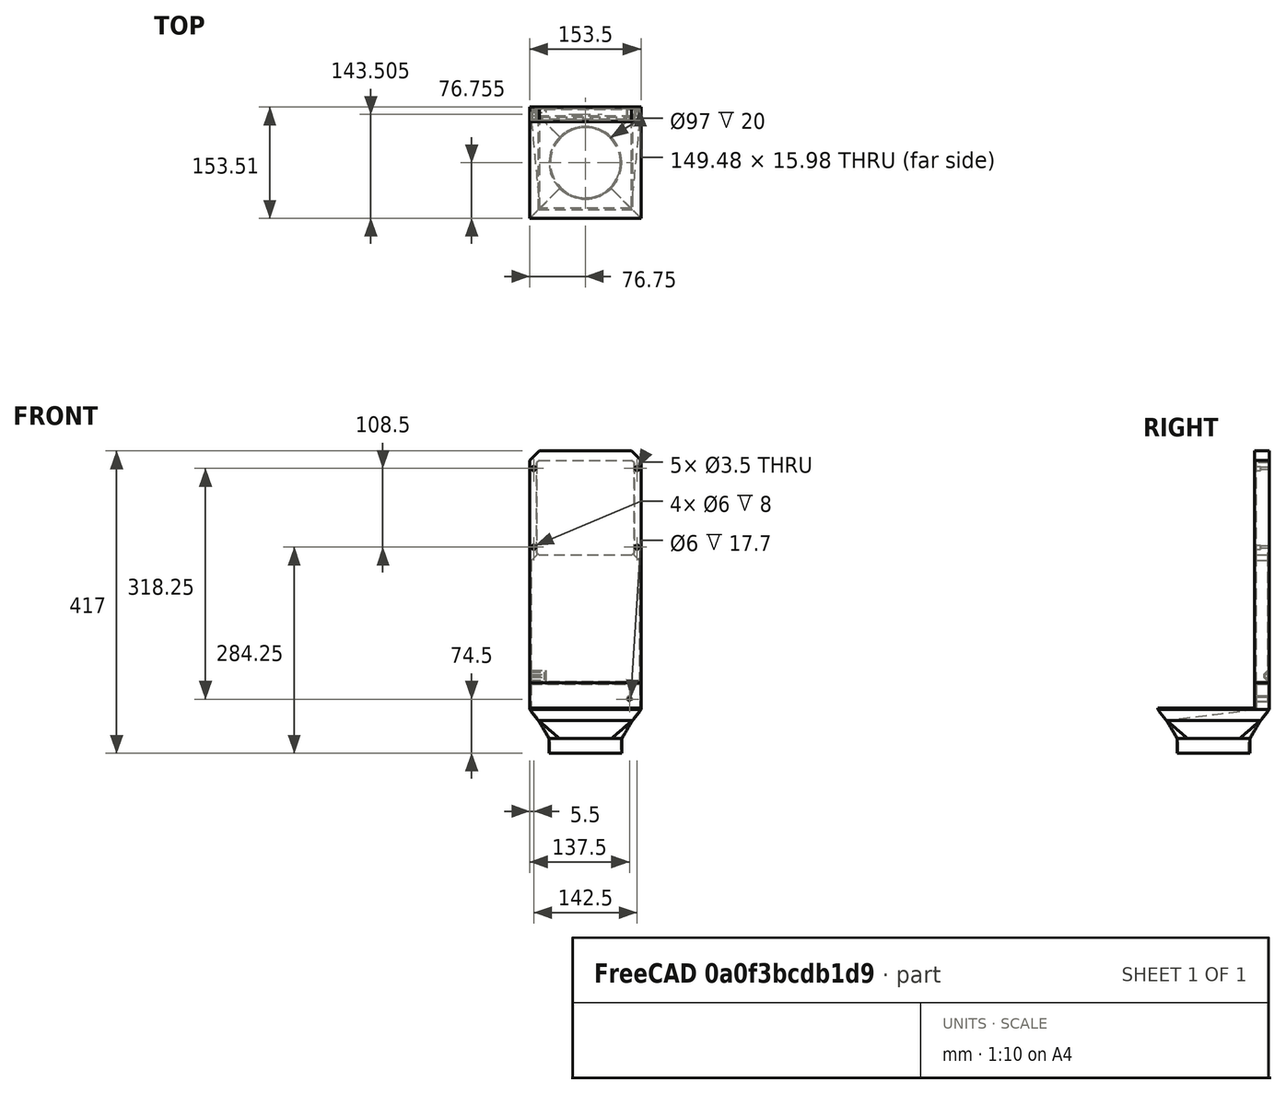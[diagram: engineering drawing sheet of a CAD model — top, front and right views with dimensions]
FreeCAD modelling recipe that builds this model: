
FCSTD DOCUMENT  (FreeCAD 1.1R20260108 (Git shallow))
Label: H2C Vertical Exhaust
License: Creative Commons Attribution 4.0
LicenseURL: https://creativecommons.org/licenses/by/4.0/
objects: Sketcher::SketchObject×14, PartDesign::Pad×9, PartDesign::Pocket×5, App::Point×3, PartDesign::Body×2, PartDesign::Chamfer×2, PartDesign::AdditiveLoft×2, App::Link×2, App::FeaturePython×2, Part::FeaturePython×2, PartDesign::SubShapeBinder×1, PartDesign::Plane×1, Assembly::JointGroup×1, Assembly::AssemblyObject×1, App::VarSet×1
note: 88 computed .brp shape members not serialized (recipe doc carries the construction recipe); baked Part::Feature solids carry a one-line shape summary decoded from their .brp

FEATURE [Sketcher::SketchObject] Sketch
  ArcFitTolerance = 1e-06
  AttachmentSupport = -> [XZ_Plane]
  ExternalTypes = [0]
  FullyConstrained = true
  MakeInternals = false
  MapMode = 5
  Placement = pos=(0,0,0) rot=(1,0,0;1.5708rad)
  sketch-geometry (25):
    g0: LineSegment StartX=-76.75 StartY=-241.5 StartZ=0 EndX=76.75 EndY=-241.5 EndZ=0
    g1: LineSegment StartX=76.75 StartY=-241.5 StartZ=0 EndX=76.75 EndY=65.5 EndZ=0
    g2: LineSegment StartX=63.75 StartY=78.5 StartZ=0 EndX=-63.75 EndY=78.5 EndZ=0
    g3: LineSegment StartX=-76.75 StartY=65.5 StartZ=0 EndX=-76.75 EndY=-241.5 EndZ=0
    g4: GeomPoint X=0 Y=0 Z=0
    g5: GeomPoint X=-76.75 Y=78.5 Z=0
    g6: GeomPoint X=76.75 Y=78.5 Z=0
    g7: LineSegment StartX=-63.75 StartY=-65.5 StartZ=0 EndX=63.75 EndY=-65.5 EndZ=0
    g8: LineSegment StartX=67.25 StartY=-62 StartZ=0 EndX=67.25 EndY=62 EndZ=0
    g9: LineSegment StartX=63.75 StartY=65.5 StartZ=0 EndX=-63.75 EndY=65.5 EndZ=0
    g10: LineSegment StartX=-67.25 StartY=62 StartZ=0 EndX=-67.25 EndY=-62 EndZ=0
    g11: GeomPoint X=0 Y=0 Z=0
    g12: GeomPoint X=-67.25 Y=65.5 Z=0
    g13: GeomPoint X=67.25 Y=65.5 Z=0
    g14: GeomPoint X=67.25 Y=-62 Z=0
    g15: Circle CenterX=-71.25 CenterY=54.25 CenterZ=0 NormalX=0 NormalY=0 NormalZ=1 AngleXU=0 Radius=1.75
    g16: Circle CenterX=71.25 CenterY=54.25 CenterZ=0 NormalX=0 NormalY=0 NormalZ=1 AngleXU=0 Radius=1.75
    g17: Circle CenterX=71.25 CenterY=-54.25 CenterZ=0 NormalX=0 NormalY=0 NormalZ=1 AngleXU=0 Radius=1.75
    g18: Circle CenterX=-71.25 CenterY=-54.25 CenterZ=0 NormalX=0 NormalY=0 NormalZ=1 AngleXU=0 Radius=1.75
    g19: LineSegment StartX=-76.75 StartY=65.5 StartZ=0 EndX=-63.75 EndY=78.5 EndZ=0
    g20: LineSegment StartX=63.75 StartY=78.5 StartZ=0 EndX=76.75 EndY=65.5 EndZ=0
    g21: LineSegment StartX=-67.25 StartY=62 StartZ=0 EndX=-63.75 EndY=65.5 EndZ=0
    g22: LineSegment StartX=63.75 StartY=65.5 StartZ=0 EndX=67.25 EndY=62 EndZ=0
    g23: LineSegment StartX=-67.25 StartY=-62 StartZ=0 EndX=-63.75 EndY=-65.5 EndZ=0
    g24: LineSegment StartX=63.75 StartY=-65.5 StartZ=0 EndX=67.25 EndY=-62 EndZ=0
  constraints (59):
    c: Horizontal(g0)
    c: Vertical(g3)
    c: Coincident(g4,g-1)
    c: DistanceX(g5,g6) = 153.5
    c: PointOnObject(g5,g3)
    c: PointOnObject(g5,g2)
    c: PointOnObject(g6,g2)
    c: PointOnObject(g6,g1)
    c: Horizontal(g7)
    c: Coincident(g11,g4)
    c: DistanceX(g12,g13) = 134.5
    c: DistanceY(g14,g13) = 127.5
    c: PointOnObject(g12,g10)
    c: PointOnObject(g12,g9)
    c: PointOnObject(g13,g9)
    c: PointOnObject(g13,g8)
    c: Horizontal(g15,g16)
    c: Horizontal(g18,g17)
    c: Vertical(g16,g17)
    c: Vertical(g15,g18)
    c: DistanceX(g15,g16) = 142.5
    c: DistanceY(g17,g16) = 108.5
    c: Symmetric(g18,g16,g4)
    c: Equal(g15,g16)
    c: Equal(g15,g18)
    c: Equal(g15,g17)
    c: Diameter(g15) = 3.5
    c: Vertical(g10)
    c: Coincident(g14,g8)
    c: Coincident(g1,g0)
    c: Coincident(g0,g3)
    c: DistanceY(g0,g2) = 320
    c: Coincident(g19,g3)
    c: Coincident(g19,g2)
    c: Coincident(g20,g2)
    c: Coincident(g20,g1)
    c: Symmetric(g2,g2,g-2)
    c: Symmetric(g3,g1,g-2)
    c: DistanceX(g3,g9) = 13
    c: Horizontal(g3,g9)
    c: Vertical(g2,g9)
    c: Coincident(g21,g10)
    c: Coincident(g21,g9)
    c: Coincident(g22,g9)
    c: Coincident(g22,g8)
    c: Angle(g19,g3) = 0.785398
    c: Angle(g21,g10) = 0.785398
    c: Symmetric(g9,g9,g-2)
    c: Symmetric(g8,g10,g-2)
    c: Vertical(g7,g9)
    c: Coincident(g23,g10)
    c: Coincident(g23,g7)
    c: Coincident(g24,g7)
    c: Coincident(g24,g8)
    c: Vertical(g7,g9)
    c: Horizontal(g10,g8)
    c: Angle(g10,g23) = 0.785398
    c: Symmetric(g8,g10,g4)
    c: Vertical(g1)
FEATURE [PartDesign::Pad] Pad  label="Surface against printer"
  Direction = (0,-1,2e-16)
  Length = 2
  Length2 = 10
  Placement = pos=(0,0,0) rot=(1,0,0;1.5708rad)
  Profile = -> Sketch
  ReferenceAxis = -> Sketch [N_Axis]
  SideType = 0
  Suppressed = false
  Type = 0
  Type2 = 0
FEATURE [Sketcher::SketchObject] Sketch011
  ArcFitTolerance = 1e-06
  AttachmentSupport = -> [Pad]
  ExternalGeometry = -> [Pad]
  ExternalTypes = [0]
  FullyConstrained = true
  MakeInternals = false
  MapMode = 5
  Placement = pos=(0,-1.17e-14,0) rot=(-1,0,0;1.5708rad)
  sketch-geometry (16):
    g0: LineSegment StartX=-76.75 StartY=-65.5 StartZ=0 EndX=-76.75 EndY=241.5 EndZ=0
    g1: LineSegment StartX=-76.75 StartY=241.5 StartZ=0 EndX=-74.75 EndY=241.5 EndZ=0
    g2: LineSegment StartX=-74.75 StartY=241.5 StartZ=0 EndX=-74.75 EndY=73 EndZ=0
    g3: LineSegment StartX=-74.75 StartY=73 StartZ=0 EndX=-67.25 EndY=65.5 EndZ=0
    g4: LineSegment StartX=-67.25 StartY=65.5 StartZ=0 EndX=-67.25 EndY=-62 EndZ=0
    g5: LineSegment StartX=-67.25 StartY=-62 StartZ=0 EndX=-63.75 EndY=-65.5 EndZ=0
    g6: LineSegment StartX=-63.75 StartY=-65.5 StartZ=0 EndX=63.75 EndY=-65.5 EndZ=0
    g7: LineSegment StartX=63.75 StartY=-65.5 StartZ=0 EndX=67.25 EndY=-62 EndZ=0
    g8: LineSegment StartX=67.25 StartY=-62 StartZ=0 EndX=67.25 EndY=65.5 EndZ=0
    g9: LineSegment StartX=67.25 StartY=65.5 StartZ=0 EndX=74.75 EndY=73 EndZ=0
    g10: LineSegment StartX=74.75 StartY=73 StartZ=0 EndX=74.75 EndY=241.5 EndZ=0
    g11: LineSegment StartX=74.75 StartY=241.5 StartZ=0 EndX=76.75 EndY=241.5 EndZ=0
    g12: LineSegment StartX=76.75 StartY=241.5 StartZ=0 EndX=76.75 EndY=-65.5 EndZ=0
    g13: LineSegment StartX=76.75 StartY=-65.5 StartZ=0 EndX=63.75 EndY=-78.5 EndZ=0
    g14: LineSegment StartX=63.75 StartY=-78.5 StartZ=0 EndX=-63.75 EndY=-78.5 EndZ=0
    g15: LineSegment StartX=-63.75 StartY=-78.5 StartZ=0 EndX=-76.75 EndY=-65.5 EndZ=0
  constraints (38):
    c: Coincident(g-6,g0)
    c: Coincident(g0,g-7)
    c: Coincident(g0,g1)
    c: PointOnObject(g1,g-7)
    c: Coincident(g1,g2)
    c: Vertical(g2)
    c: Coincident(g2,g3)
    c: Coincident(g3,g4)
    c: Coincident(g4,g-3)
    c: PointOnObject(g-3,g4)
    c: DistanceX(g1,g1) = 2
    c: Angle(g2,g3) = 0.785398
    c: PointOnObject(g3,g-8)
    c: Coincident(g4,g5)
    c: Coincident(g5,g-9)
    c: Coincident(g5,g6)
    c: Coincident(g6,g-9)
    c: Coincident(g6,g7)
    c: Coincident(g7,g-4)
    c: Coincident(g7,g8)
    c: Vertical(g8)
    c: Coincident(g8,g9)
    c: Coincident(g9,g10)
    c: PointOnObject(g10,g-7)
    c: Vertical(g10)
    c: Coincident(g10,g11)
    c: Coincident(g11,g-7)
    c: Coincident(g11,g12)
    c: Coincident(g12,g-5)
    c: Coincident(g12,g13)
    c: Coincident(g13,g-5)
    c: Coincident(g13,g14)
    c: Coincident(g14,g-6)
    c: Coincident(g14,g15)
    c: Coincident(g15,g0)
    c: Angle(g9,g10) = 0.785398
    c: PointOnObject(g8,g-8)
    c: Equal(g11,g1)
FEATURE [PartDesign::Pad] Pad006  label="Duct walls"
  BaseFeature = -> Pad
  Direction = (0,1,2e-16)
  Length = 16
  Length2 = 10
  Placement = pos=(0,0,0) rot=(1,0,0;1.5708rad)
  Profile = -> Sketch011
  ReferenceAxis = -> Sketch011 [N_Axis]
  Refine = true
  SideType = 0
  Suppressed = false
  Type = 0
  Type2 = 0
FEATURE [Sketcher::SketchObject] Sketch012
  ArcFitTolerance = 1e-06
  AttachmentSupport = -> [Pad006]
  ExternalGeometry = -> [Pad006]
  ExternalTypes = [0]
  FullyConstrained = true
  MakeInternals = false
  MapMode = 5
  Placement = pos=(0,16,0) rot=(-1,0,0;1.5708rad)
  sketch-geometry (6):
    g0: LineSegment StartX=-76.75 StartY=241.5 StartZ=0 EndX=-76.75 EndY=-65.5 EndZ=0
    g1: LineSegment StartX=-76.75 StartY=-65.5 StartZ=0 EndX=-63.75 EndY=-78.5 EndZ=0
    g2: LineSegment StartX=-63.75 StartY=-78.5 StartZ=0 EndX=63.75 EndY=-78.5 EndZ=0
    g3: LineSegment StartX=63.75 StartY=-78.5 StartZ=0 EndX=76.75 EndY=-65.5 EndZ=0
    g4: LineSegment StartX=76.75 StartY=-65.5 StartZ=0 EndX=76.75 EndY=241.5 EndZ=0
    g5: LineSegment StartX=76.75 StartY=241.5 StartZ=0 EndX=-76.75 EndY=241.5 EndZ=0
  constraints (12):
    c: Coincident(g-3,g0)
    c: Coincident(g0,g-3)
    c: Coincident(g0,g1)
    c: Coincident(g1,g-5)
    c: Coincident(g1,g2)
    c: Coincident(g2,g-5)
    c: Coincident(g2,g3)
    c: Coincident(g3,g-4)
    c: Coincident(g3,g4)
    c: Coincident(g4,g-4)
    c: Coincident(g4,g5)
    c: Coincident(g5,g0)
FEATURE [PartDesign::Pad] Pad007  label="Surface away from printer"
  BaseFeature = -> Pad006
  Direction = (0,1,2e-16)
  Length = 2
  Length2 = 10
  Placement = pos=(0,0,0) rot=(1,0,0;1.5708rad)
  Profile = -> Sketch012
  ReferenceAxis = -> Sketch012 [N_Axis]
  Refine = true
  SideType = 0
  Suppressed = false
  Type = 0
  Type2 = 0
FEATURE [Sketcher::SketchObject] Sketch003
  ArcFitTolerance = 1e-06
  AttachmentOffset = pos=(0,0,6) rot=(0,0,1;0rad)
  AttachmentSupport = -> [Pad007]
  ExternalTypes = [0]
  FullyConstrained = true
  MakeInternals = false
  MapMode = 5
  Placement = pos=(0,10,1.3e-15) rot=(1,0,0;1.5708rad)
  sketch-geometry (4):
    g0: Circle CenterX=71.25 CenterY=54.25 CenterZ=0 NormalX=0 NormalY=0 NormalZ=1 AngleXU=0 Radius=3
    g1: Circle CenterX=-71.25 CenterY=54.25 CenterZ=0 NormalX=0 NormalY=0 NormalZ=1 AngleXU=0 Radius=3
    g2: Circle CenterX=-71.25 CenterY=-54.25 CenterZ=0 NormalX=0 NormalY=0 NormalZ=1 AngleXU=0 Radius=3
    g3: Circle CenterX=71.25 CenterY=-54.25 CenterZ=0 NormalX=0 NormalY=0 NormalZ=1 AngleXU=0 Radius=3
  constraints (8):
    c: Coincident(g0,g-4)
    c: Coincident(g1,g-3)
    c: Coincident(g2,g-6)
    c: Coincident(g3,g-5)
    c: Equal(g3,g2)
    c: Equal(g0,g1)
    c: Equal(g1,g2)
    c: Diameter(g3) = 6
FEATURE [PartDesign::Pocket] Pocket  label="Screw head pockets"
  BaseFeature = -> Pad007
  Direction = (0,1,-2e-16)
  Length = 5
  Length2 = 5
  Placement = pos=(0,0,0) rot=(1,0,0;1.5708rad)
  Profile = -> Sketch003
  ReferenceAxis = -> Sketch003 [N_Axis]
  SideType = 0
  Suppressed = false
  Type = 1
  Type2 = 0
FEATURE [PartDesign::Pocket] Pocket001  label="Screw pockets"
  BaseFeature = -> Pocket
  Direction = (0,-1,0)
  Length = 5
  Length2 = 5
  Placement = pos=(0,0,0) rot=(1,0,0;1.5708rad)
  Profile = -> Pocket [Edge44,Edge45,Edge46,Edge43]
  Reversed = true
  SideType = 0
  Suppressed = false
  Type = 1
  Type2 = 0
FEATURE [Sketcher::SketchObject] Sketch013
  ArcFitTolerance = 1e-06
  AttachmentSupport = -> [Pocket001]
  ExternalGeometry = -> [Pocket001]
  ExternalTypes = [0]
  FullyConstrained = true
  MakeInternals = false
  MapMode = 5
  Placement = pos=(76.75,0,0) rot=(0.707107,0,0.707107;3.14159rad)
  sketch-geometry (7):
    g0: LineSegment StartX=-239.5 StartY=2 StartZ=0 EndX=-239.5 EndY=1.572e-13 EndZ=0
    g1: LineSegment StartX=-239.5 StartY=1.572e-13 StartZ=0 EndX=-234 EndY=-5.5 EndZ=0
    g2: LineSegment StartX=-234 StartY=-5.5 StartZ=0 EndX=-230 EndY=-5.5 EndZ=0
    g3: LineSegment StartX=-230 StartY=-5.5 StartZ=0 EndX=-224.5 EndY=1.572e-13 EndZ=0
    g4: LineSegment StartX=-224.5 StartY=1.572e-13 StartZ=0 EndX=-224.5 EndY=2 EndZ=0
    g5: LineSegment StartX=-224.5 StartY=2 StartZ=0 EndX=-239.5 EndY=2 EndZ=0
    g6: GeomPoint X=-54.25 Y=2 Z=0
  constraints (19):
    c: PointOnObject(g0,g-4)
    c: Vertical(g0)
    c: Coincident(g0,g1)
    c: Coincident(g1,g2)
    c: Horizontal(g2)
    c: Coincident(g2,g3)
    c: Coincident(g3,g4)
    c: PointOnObject(g4,g-4)
    c: Vertical(g4)
    c: Coincident(g4,g5)
    c: Coincident(g5,g0)
    c: Angle(g0,g1) = 0.785398
    c: Angle(g3,g4) = 0.785398
    c: DistanceX(g5,g5) = 15
    c: DistanceY(g2,g4) = 7.5
    c: DistanceY(g4,g4) = 2
    c: Symmetric(g-3,g-3,g6)
    c: Horizontal(g0,g3)
    c: DistanceX(g4,g6) = 170.25
FEATURE [PartDesign::Pad] Pad008  label="Filament tube walls"
  BaseFeature = -> Pocket001
  Direction = (1,0,-2e-16)
  Length = 22
  Length2 = 10
  Placement = pos=(0,0,0) rot=(1,0,0;1.5708rad)
  Profile = -> Sketch013
  ReferenceAxis = -> Sketch013 [N_Axis]
  Refine = true
  Reversed = true
  SideType = 0
  Suppressed = false
  Type = 0
  Type2 = 0
FEATURE [Sketcher::SketchObject] Sketch014
  ArcFitTolerance = 1e-06
  AttachmentSupport = -> [Pad008]
  ExternalGeometry = -> [Sketch013]
  ExternalTypes = [0]
  FullyConstrained = true
  MakeInternals = false
  MapMode = 5
  Placement = pos=(76.75,0,0) rot=(0.707107,0,0.707107;3.14159rad)
  sketch-geometry (7):
    g0: LineSegment StartX=-237.5 StartY=2 StartZ=0 EndX=-237.5 EndY=0.828427 EndZ=0
    g1: LineSegment StartX=-237.5 StartY=0.828427 StartZ=0 EndX=-233.172 EndY=-3.5 EndZ=0
    g2: LineSegment StartX=-233.172 StartY=-3.5 StartZ=0 EndX=-230.828 EndY=-3.5 EndZ=0
    g3: LineSegment StartX=-230.828 StartY=-3.5 StartZ=0 EndX=-226.5 EndY=0.828427 EndZ=0
    g4: LineSegment StartX=-226.5 StartY=0.828427 StartZ=0 EndX=-226.5 EndY=2 EndZ=0
    g5: LineSegment StartX=-226.5 StartY=2 StartZ=0 EndX=-237.5 EndY=2 EndZ=0
    g6: LineSegment StartX=-230 StartY=-5.5 StartZ=0 EndX=-230.828 EndY=-3.5 EndZ=0
  constraints (20):
    c: PointOnObject(g0,g-3)
    c: Vertical(g0)
    c: Coincident(g0,g1)
    c: Coincident(g1,g2)
    c: Horizontal(g2)
    c: Coincident(g2,g3)
    c: Coincident(g3,g4)
    c: PointOnObject(g4,g-3)
    c: Vertical(g4)
    c: Coincident(g4,g5)
    c: Coincident(g5,g0)
    c: Angle(g0,g1) = 0.785398
    c: Angle(g3,g4) = 0.785398
    c: DistanceX(g-3,g0) = 2
    c: DistanceX(g4,g-3) = 2
    c: DistanceY(g-4,g2) = 2
    c: Horizontal(g0,g3)
    c: Coincident(g6,g-4)
    c: Coincident(g6,g2)
    c: Angle(g6,g-4) = 1.1781
FEATURE [PartDesign::Pocket] Pocket002  label="Filament tube opening"
  BaseFeature = -> Pad008
  Direction = (-1,0,2e-16)
  Length = 20
  Length2 = 5
  Placement = pos=(0,0,0) rot=(1,0,0;1.5708rad)
  Profile = -> Sketch014 [Edge3,Edge2,Edge1,Edge7,Edge6,Edge5]
  ReferenceAxis = -> Sketch014 [N_Axis]
  SideType = 0
  Suppressed = false
  Type = 0
  Type2 = 0
FEATURE [PartDesign::Body] Body  label="Back of printer"
  AllowCompound = false
  Group = -> [Sketch,Pad,Pad006,Pad007,Pocket,Pocket001,Sketch003,Sketch011,Sketch012,Sketch013,Pad008,Sketch014,Pocket002]
  Origin = -> Origin
  Placement = pos=(2e-15,15.975,0) rot=(0,0,1;3.14159rad)
  Tip = -> Pocket002
FEATURE [PartDesign::SubShapeBinder] Binder  label="Duct opening binder"
  BindCopyOnChange = 0
  BindMode = 0
  ClaimChildren = false
  Context = -> Body001 [Binder.]
  Fuse = false
  MakeFace = true
  OffsetFill = false
  OffsetIntersection = false
  OffsetJoinType = 0
  OffsetOpenResult = false
  PartialLoad = false
  Relative = true
  Support = -> [Body[Pocket002.Face3]]
  _Version = 2
FEATURE [PartDesign::Plane] DatumPlane  label="Duct opening plane"
  AttachmentSupport = -> [Binder]
  Length = 184.895
  MapMode = 13
  Placement = pos=(25.5833,4.64167,-241.5) rot=(0,0,1;0rad)
  ResizeMode = 0
  Width = 191.92
FEATURE [Sketcher::SketchObject] Sketch015
  ArcFitTolerance = 1e-06
  AttachmentSupport = -> [DatumPlane]
  ExternalGeometry = -> [Binder]
  ExternalTypes = [0]
  FullyConstrained = true
  MakeInternals = false
  MapMode = 5
  Placement = pos=(25.5833,4.64167,-241.5) rot=(0,0,1;0rad)
  sketch-geometry (8):
    g0: LineSegment StartX=49.1667 StartY=-4.66667 StartZ=0 EndX=49.1667 EndY=11.3333 EndZ=0
    g1: LineSegment StartX=49.1667 StartY=11.3333 StartZ=0 EndX=-100.333 EndY=11.3333 EndZ=0
    g2: LineSegment StartX=-100.333 StartY=11.3333 StartZ=0 EndX=-100.333 EndY=-4.66667 EndZ=0
    g3: LineSegment StartX=-100.333 StartY=-4.66667 StartZ=0 EndX=49.1667 EndY=-4.66667 EndZ=0
    g4: LineSegment StartX=51.1667 StartY=-6.66667 StartZ=0 EndX=51.1667 EndY=13.3333 EndZ=0
    g5: LineSegment StartX=51.1667 StartY=13.3333 StartZ=0 EndX=-102.333 EndY=13.3333 EndZ=0
    g6: LineSegment StartX=-102.333 StartY=13.3333 StartZ=0 EndX=-102.333 EndY=-6.66667 EndZ=0
    g7: LineSegment StartX=-102.333 StartY=-6.66667 StartZ=0 EndX=51.1667 EndY=-6.66667 EndZ=0
  constraints (20):
    c: Coincident(g0,g1)
    c: Coincident(g1,g2)
    c: Coincident(g2,g3)
    c: Coincident(g3,g0)
    c: Vertical(g0)
    c: Vertical(g2)
    c: Horizontal(g1)
    c: Horizontal(g3)
    c: Coincident(g0,g-4)
    c: Coincident(g1,g-5)
    c: Coincident(g4,g5)
    c: Coincident(g5,g6)
    c: Coincident(g6,g7)
    c: Coincident(g7,g4)
    c: Vertical(g4)
    c: Vertical(g6)
    c: Horizontal(g5)
    c: Horizontal(g7)
    c: Coincident(g4,g-3)
    c: Coincident(g5,g-6)
FEATURE [PartDesign::Pad] Pad009  label="Tube extension to top of printer"
  Direction = (0,-4.3e-15,1)
  Length = 35
  Length2 = 10
  Placement = pos=(25.5833,4.64167,-241.5) rot=(0,0,1;0rad)
  Profile = -> Sketch015
  ReferenceAxis = -> Sketch015 [N_Axis]
  Reversed = true
  SideType = 0
  Suppressed = false
  Type = 0
  Type2 = 0
FEATURE [Sketcher::SketchObject] Sketch016
  ArcFitTolerance = 1e-06
  AttachmentSupport = -> [Pad009]
  ExternalGeometry = -> [Pad009]
  ExternalTypes = [0]
  FullyConstrained = true
  MakeInternals = false
  MapMode = 5
  Placement = pos=(25.5833,4.64167,-241.5) rot=(0,0,1;0rad)
  sketch-geometry (9):
    g0: LineSegment StartX=49.1667 StartY=-4.66667 StartZ=0 EndX=49.1667 EndY=11.3333 EndZ=0
    g1: LineSegment StartX=49.1667 StartY=11.3333 StartZ=0 EndX=-100.333 EndY=11.3333 EndZ=0
    g2: LineSegment StartX=-100.333 StartY=11.3333 StartZ=0 EndX=-100.333 EndY=-4.66667 EndZ=0
    g3: LineSegment StartX=-100.333 StartY=-4.66667 StartZ=0 EndX=49.1667 EndY=-4.66667 EndZ=0
    g4: LineSegment StartX=47.6667 StartY=-3.16667 StartZ=0 EndX=47.6667 EndY=9.83333 EndZ=0
    g5: LineSegment StartX=47.6667 StartY=9.83333 StartZ=0 EndX=-98.8333 EndY=9.83333 EndZ=0
    g6: LineSegment StartX=-98.8333 StartY=9.83333 StartZ=0 EndX=-98.8333 EndY=-3.16667 EndZ=0
    g7: LineSegment StartX=-98.8333 StartY=-3.16667 StartZ=0 EndX=47.6667 EndY=-3.16667 EndZ=0
    g8: GeomPoint X=-25.5833 Y=3.33333 Z=0
  constraints (22):
    c: Coincident(g0,g1)
    c: Coincident(g1,g2)
    c: Coincident(g2,g3)
    c: Coincident(g3,g0)
    c: Vertical(g0)
    c: Vertical(g2)
    c: Horizontal(g1)
    c: Horizontal(g3)
    c: Coincident(g0,g-3)
    c: Coincident(g1,g-4)
    c: Coincident(g4,g5)
    c: Coincident(g5,g6)
    c: Coincident(g6,g7)
    c: Coincident(g7,g4)
    c: Vertical(g4)
    c: Vertical(g6)
    c: Horizontal(g5)
    c: Horizontal(g7)
    c: Symmetric(g0,g1,g8)
    c: Symmetric(g4,g5,g8)
    c: DistanceX(g1,g5) = 1.5
    c: DistanceY(g5,g1) = 1.5
FEATURE [PartDesign::Pad] Pad010  label="Connector"
  BaseFeature = -> Pad009
  Direction = (0,-8.9e-15,1)
  Length = 4
  Length2 = 10
  Placement = pos=(25.5833,4.64167,-241.5) rot=(0,0,1;0rad)
  Profile = -> Sketch016
  ReferenceAxis = -> Sketch016 [N_Axis]
  SideType = 2
  Suppressed = false
  Type = 0
  Type2 = 0
FEATURE [PartDesign::Chamfer] Chamfer  label="Connector chamfer 1"
  Angle = 45
  Base = -> Pad010 [Edge28,Edge22,Edge27,Edge25]
  BaseFeature = -> Pad010
  ChamferType = 0
  FlipDirection = false
  Placement = pos=(25.5833,4.64167,-241.5) rot=(0,0,1;0rad)
  Size = 0.75
  Size2 = 1
  SupportTransform = false
  Suppressed = false
  UseAllEdges = false
FEATURE [PartDesign::Chamfer] Chamfer001  label="Connector chamfer 2"
  Angle = 45
  Base = -> Chamfer [Edge43,Edge44,Edge39,Edge41]
  BaseFeature = -> Chamfer
  ChamferType = 0
  FlipDirection = false
  Placement = pos=(25.5833,4.64167,-241.5) rot=(0,0,1;0rad)
  Size = 1.49
  Size2 = 1
  SupportTransform = false
  Suppressed = false
  UseAllEdges = false
FEATURE [Sketcher::SketchObject] Sketch017
  ArcFitTolerance = 1e-06
  AttachmentSupport = -> [Chamfer001]
  ExternalGeometry = -> [Chamfer001]
  ExternalTypes = [0]
  FullyConstrained = true
  MakeInternals = false
  MapMode = 5
  Placement = pos=(25.5833,4.64167,-276.5) rot=(1,0,0;3.14159rad)
  sketch-geometry (8):
    g0: LineSegment StartX=49.1667 StartY=-11.3333 StartZ=0 EndX=49.1667 EndY=4.66667 EndZ=0
    g1: LineSegment StartX=49.1667 StartY=4.66667 StartZ=0 EndX=-100.333 EndY=4.66667 EndZ=0
    g2: LineSegment StartX=-100.333 StartY=4.66667 StartZ=0 EndX=-100.333 EndY=-11.3333 EndZ=0
    g3: LineSegment StartX=-100.333 StartY=-11.3333 StartZ=0 EndX=49.1667 EndY=-11.3333 EndZ=0
    g4: LineSegment StartX=51.1667 StartY=-13.3333 StartZ=0 EndX=51.1667 EndY=140.167 EndZ=0
    g5: LineSegment StartX=51.1667 StartY=140.167 StartZ=0 EndX=-102.333 EndY=140.167 EndZ=0
    g6: LineSegment StartX=-102.333 StartY=140.167 StartZ=0 EndX=-102.333 EndY=-13.3333 EndZ=0
    g7: LineSegment StartX=-102.333 StartY=-13.3333 StartZ=0 EndX=51.1667 EndY=-13.3333 EndZ=0
  constraints (20):
    c: Coincident(g0,g1)
    c: Coincident(g1,g2)
    c: Coincident(g2,g3)
    c: Coincident(g3,g0)
    c: Vertical(g0)
    c: Vertical(g2)
    c: Horizontal(g1)
    c: Horizontal(g3)
    c: Coincident(g0,g-5)
    c: Coincident(g1,g-6)
    c: Coincident(g4,g5)
    c: Coincident(g5,g6)
    c: Coincident(g6,g7)
    c: Coincident(g7,g4)
    c: Vertical(g4)
    c: Vertical(g6)
    c: Horizontal(g5)
    c: Coincident(g4,g-3)
    c: Coincident(g6,g-4)
    c: Equal(g4,g7)
FEATURE [PartDesign::Pad] Pad011  label="Surface against top of printer"
  BaseFeature = -> Chamfer001
  Direction = (0,1.32e-14,-1)
  Length = 2
  Length2 = 10
  Placement = pos=(25.5833,4.64167,-241.5) rot=(0,0,1;0rad)
  Profile = -> Sketch017
  ReferenceAxis = -> Sketch017 [N_Axis]
  SideType = 0
  Suppressed = false
  Type = 0
  Type2 = 0
FEATURE [Sketcher::SketchObject] Sketch018
  ArcFitTolerance = 1e-06
  AttachmentOffset = pos=(0,0,40) rot=(0,0,1;0rad)
  AttachmentSupport = -> [Pad011]
  ExternalGeometry = -> [Pad011]
  ExternalTypes = [0]
  FullyConstrained = true
  MakeInternals = false
  MapMode = 5
  Placement = pos=(25.5833,4.64167,-318.5) rot=(1,0,0;3.14159rad)
  expr: Constraints[3] = VarSet.Diameter - 3 mm
  expr: Constraints[4] = VarSet.Diameter
  sketch-geometry (3):
    g0: GeomPoint X=-25.5833 Y=63.4167 Z=0
    g1: Circle CenterX=-25.5833 CenterY=63.4167 CenterZ=0 NormalX=0 NormalY=0 NormalZ=1 AngleXU=0 Radius=50
    g2: Circle CenterX=-25.5833 CenterY=63.4167 CenterZ=0 NormalX=0 NormalY=0 NormalZ=1 AngleXU=0 Radius=48.5
  constraints (5):
    c: Symmetric(g-3,g-4,g0)
    c: Coincident(g1,g0)
    c: Coincident(g2,g0)
    c: Diameter(g2) = 97
    c: Diameter(g1) = 100
FEATURE [Sketcher::SketchObject] Sketch019
  ArcFitTolerance = 1e-06
  AttachmentOffset = pos=(0,0,15) rot=(0,0,1;0rad)
  AttachmentSupport = -> [Pad011]
  ExternalGeometry = -> [Pad011]
  ExternalTypes = [0]
  FullyConstrained = true
  MakeInternals = false
  MapMode = 5
  Placement = pos=(25.5833,4.64167,-293.5) rot=(1,0,0;3.14159rad)
  sketch-geometry (11):
    g0: GeomPoint X=-25.5833 Y=63.4167 Z=0
    g1: LineSegment StartX=-90.5833 StartY=-1.58333 StartZ=0 EndX=39.4167 EndY=-1.58333 EndZ=0
    g2: LineSegment StartX=39.4167 StartY=-1.58333 StartZ=0 EndX=39.4167 EndY=128.417 EndZ=0
    g3: LineSegment StartX=39.4167 StartY=128.417 StartZ=0 EndX=-90.5833 EndY=128.417 EndZ=0
    g4: LineSegment StartX=-90.5833 StartY=128.417 StartZ=0 EndX=-90.5833 EndY=-1.58333 EndZ=0
    g5: GeomPoint X=-25.5833 Y=63.4167 Z=0
    g6: LineSegment StartX=-88.5833 StartY=0.416667 StartZ=0 EndX=37.4167 EndY=0.416667 EndZ=0
    g7: LineSegment StartX=37.4167 StartY=0.416667 StartZ=0 EndX=37.4167 EndY=126.417 EndZ=0
    g8: LineSegment StartX=37.4167 StartY=126.417 StartZ=0 EndX=-88.5833 EndY=126.417 EndZ=0
    g9: LineSegment StartX=-88.5833 StartY=126.417 StartZ=0 EndX=-88.5833 EndY=0.416667 EndZ=0
    g10: GeomPoint X=-25.5833 Y=63.4167 Z=0
  constraints (25):
    c: Symmetric(g-3,g-4,g0)
    c: Coincident(g1,g2)
    c: Coincident(g2,g3)
    c: Coincident(g3,g4)
    c: Coincident(g4,g1)
    c: Horizontal(g1)
    c: Horizontal(g3)
    c: Vertical(g2)
    c: Vertical(g4)
    c: Symmetric(g3,g1,g5)
    c: Coincident(g5,g0)
    c: DistanceY(g2,g2) = 130
    c: Equal(g1,g2)
    c: Coincident(g6,g7)
    c: Coincident(g7,g8)
    c: Coincident(g8,g9)
    c: Coincident(g9,g6)
    c: Horizontal(g6)
    c: Horizontal(g8)
    c: Vertical(g7)
    c: Vertical(g9)
    c: Symmetric(g8,g6,g10)
    c: Coincident(g10,g0)
    c: Equal(g7,g6)
    c: DistanceY(g8,g3) = 2
FEATURE [PartDesign::AdditiveLoft] AdditiveLoft  label="Transition to larger square opening"
  BaseFeature = -> Pad011
  Closed = false
  Placement = pos=(25.5833,4.64167,-241.5) rot=(0,0,1;0rad)
  Profile = -> Pad011 [Face28]
  Ruled = false
  Sections = -> [Sketch019]
  Suppressed = false
FEATURE [PartDesign::AdditiveLoft] AdditiveLoft001  label="Transition to circle"
  BaseFeature = -> AdditiveLoft
  Closed = false
  Placement = pos=(25.5833,4.64167,-241.5) rot=(0,0,1;0rad)
  Profile = -> AdditiveLoft [Face36]
  Ruled = false
  Sections = -> [Sketch018]
  Suppressed = false
FEATURE [PartDesign::Pad] Pad012  label="Interface with duct"
  BaseFeature = -> AdditiveLoft001
  Direction = (0,1.77e-14,-1)
  Length = 20
  Length2 = 10
  Placement = pos=(25.5833,4.64167,-241.5) rot=(0,0,1;0rad)
  Profile = -> Sketch018
  ReferenceAxis = -> Sketch018 [N_Axis]
  Refine = true
  SideType = 0
  Suppressed = false
  Type = 0
  Type2 = 0
FEATURE [Sketcher::SketchObject] Sketch020
  ArcFitTolerance = 1e-06
  AttachmentSupport = -> [Pad012]
  ExternalTypes = [0]
  FullyConstrained = true
  MakeInternals = false
  MapMode = 5
  Placement = pos=(25.5833,-2.025,-241.5) rot=(1,0,0;1.5708rad)
  sketch-geometry (1):
    g0: Circle CenterX=35.1667 CenterY=-22.5 CenterZ=0 NormalX=0 NormalY=0 NormalZ=1 AngleXU=0 Radius=4
  constraints (3):
    c: DistanceX(g0,g-3) = 16
    c: Diameter(g0) = 8
    c: DistanceY(g-3,g0) = 12.5
FEATURE [PartDesign::Pad] Pad013  label="Screw column"
  BaseFeature = -> Pad012
  Direction = (0,-1,-3e-14)
  Length = 10
  Length2 = 10
  Placement = pos=(25.5833,4.64167,-241.5) rot=(0,0,1;0rad)
  Profile = -> Sketch020
  ReferenceAxis = -> Sketch020 [N_Axis]
  Refine = true
  Reversed = true
  SideType = 0
  Suppressed = false
  Type = 3
  Type2 = 0
  UpToFace = -> Pad012 [Face49]
FEATURE [Sketcher::SketchObject] Sketch021
  ArcFitTolerance = 1e-06
  AttachmentSupport = -> [Pad013]
  ExternalGeometry = -> [Sketch020]
  ExternalTypes = [0]
  FullyConstrained = true
  MakeInternals = false
  MapMode = 5
  Placement = pos=(25.5833,-2.025,-241.5) rot=(1,0,0;1.5708rad)
  sketch-geometry (1):
    g0: Circle CenterX=35.1667 CenterY=-22.5 CenterZ=0 NormalX=0 NormalY=0 NormalZ=1 AngleXU=0 Radius=1.75
  constraints (2):
    c: Coincident(g0,g-3)
    c: Diameter(g0) = 3.5
FEATURE [PartDesign::Pocket] Pocket003  label="Screw tunnel"
  BaseFeature = -> Pad013
  Direction = (0,1,3.4e-14)
  Length = 5
  Length2 = 5
  Placement = pos=(25.5833,4.64167,-241.5) rot=(0,0,1;0rad)
  Profile = -> Sketch021
  ReferenceAxis = -> Sketch021 [N_Axis]
  SideType = 0
  Suppressed = false
  Type = 1
  Type2 = 0
FEATURE [Sketcher::SketchObject] Sketch022
  ArcFitTolerance = 1e-06
  AttachmentSupport = -> [Pocket003]
  ExternalGeometry = -> [Pocket003]
  ExternalTypes = [0]
  FullyConstrained = true
  MakeInternals = false
  MapMode = 5
  Placement = pos=(25.5833,17.975,-241.5) rot=(0,0.707107,0.707107;3.14159rad)
  sketch-geometry (1):
    g0: Circle CenterX=-35.1667 CenterY=-22.5 CenterZ=0 NormalX=0 NormalY=0 NormalZ=1 AngleXU=0 Radius=3
  constraints (2):
    c: Coincident(g0,g-3)
    c: Diameter(g0) = 6
FEATURE [PartDesign::Pocket] Pocket004  label="Screw head recess"
  BaseFeature = -> Pocket003
  Direction = (0,-1,-3.85e-14)
  Length = 17.7
  Length2 = 5
  Placement = pos=(25.5833,4.64167,-241.5) rot=(0,0,1;0rad)
  Profile = -> Sketch022
  ReferenceAxis = -> Sketch022 [N_Axis]
  SideType = 0
  Suppressed = false
  Type = 0
  Type2 = 0
FEATURE [App::Link] Back_of_printer  label="Back of printer001"
  LinkPlacement = pos=(0,0,0) rot=(0,1,0;3.14159rad)
  LinkedObject = -> Body
  Placement = pos=(0,0,0) rot=(0,1,0;3.14159rad)
FEATURE [App::FeaturePython] GroundedJoint  # Assembly grounded joint (typed FeaturePython)
  ObjectToGround = -> Back_of_printer
FEATURE [App::Link] Duct_adapter  label="Duct adapter001"
  LinkPlacement = pos=(-1.246e-13,0.025,20.3207) rot=(0,1,0;3.14159rad)
  LinkedObject = -> Body001
  Placement = pos=(-1.246e-13,0.025,20.3207) rot=(0,1,0;3.14159rad)
FEATURE [App::FeaturePython] Joint  label="Slider"  # Assembly joint (typed FeaturePython)
  Angle = 0
  AngleMax = 0
  AngleMin = 0
  Detach1 = false
  Detach2 = false
  Distance = 0
  Distance2 = 0
  EnableAngleMax = false
  EnableAngleMin = false
  EnableLengthMax = true
  EnableLengthMin = false
  JointType = 3 (Slider)
  LengthMax = 0
  LengthMin = 0
  Placement1 = pos=(-76.75,-2.025,-259) rot=(0,1,0;3.14159rad)
  Placement2 = pos=(-76.75,-2,-88) rot=(0,1,0;3.14159rad)
  Reference1 = -> Assembly [Duct_adapter.Edge90,Duct_adapter.Edge90]
  Reference2 = -> Assembly [Back_of_printer.Edge13,Back_of_printer.Edge13]
  Suppressed = false
FEATURE [Assembly::JointGroup] Joints
  Group = -> [GroundedJoint,Joint]
FEATURE [Assembly::AssemblyObject] Assembly  label="Vertical Exhaust Assembly"
  Group = -> [Joints,Back_of_printer,GroundedJoint,Duct_adapter,Joint]
  Origin = -> Origin003
  Type = Assembly
FEATURE [Part::FeaturePython] SpotLight  # WARN: FeaturePython — macro-defined, semantics opaque (R4)
  FadeDistance = 0
  FadePower = 0
  FallOff = 45
  Placement = pos=(-420.678,-390.572,568.16) rot=(0.156558,0.377964,0.912487;2.41886rad)
  Radius = 30
  Tightness = 0
FEATURE [Part::FeaturePython] AreaLight  # WARN: FeaturePython — macro-defined, semantics opaque (R4)
  Adaptive = 1
  AreaIllumination = false
  FadeDistance = 0
  FadePower = 0
  Jitter = true
  Length = 50
  LengthLights = 5
  Placement = pos=(318.75,-427,877.75) rot=(0,0,1;0rad)
  Width = 50
  WidthLights = 5
FEATURE [App::Point] Origin004  label="Origin"
  Role = Origin
FEATURE [App::Point] Origin005  label="Origin"
  Role = Origin
FEATURE [App::Point] Origin006  label="Origin"
  Role = Origin
FEATURE [App::VarSet] VarSet
  Diameter = 100
FEATURE [PartDesign::Body] Body001  label="Duct adapter"
  AllowCompound = false
  Group = -> [Binder,DatumPlane,Sketch015,Pad009,Sketch016,Pad010,Chamfer,Chamfer001,Sketch017,Pad011,Sketch019,AdditiveLoft,Sketch018,AdditiveLoft001,Pad012,Sketch020,Pad013,Sketch021,Pocket003,Sketch022,Pocket004,VarSet]
  Origin = -> Origin001
  Tip = -> Pocket004
